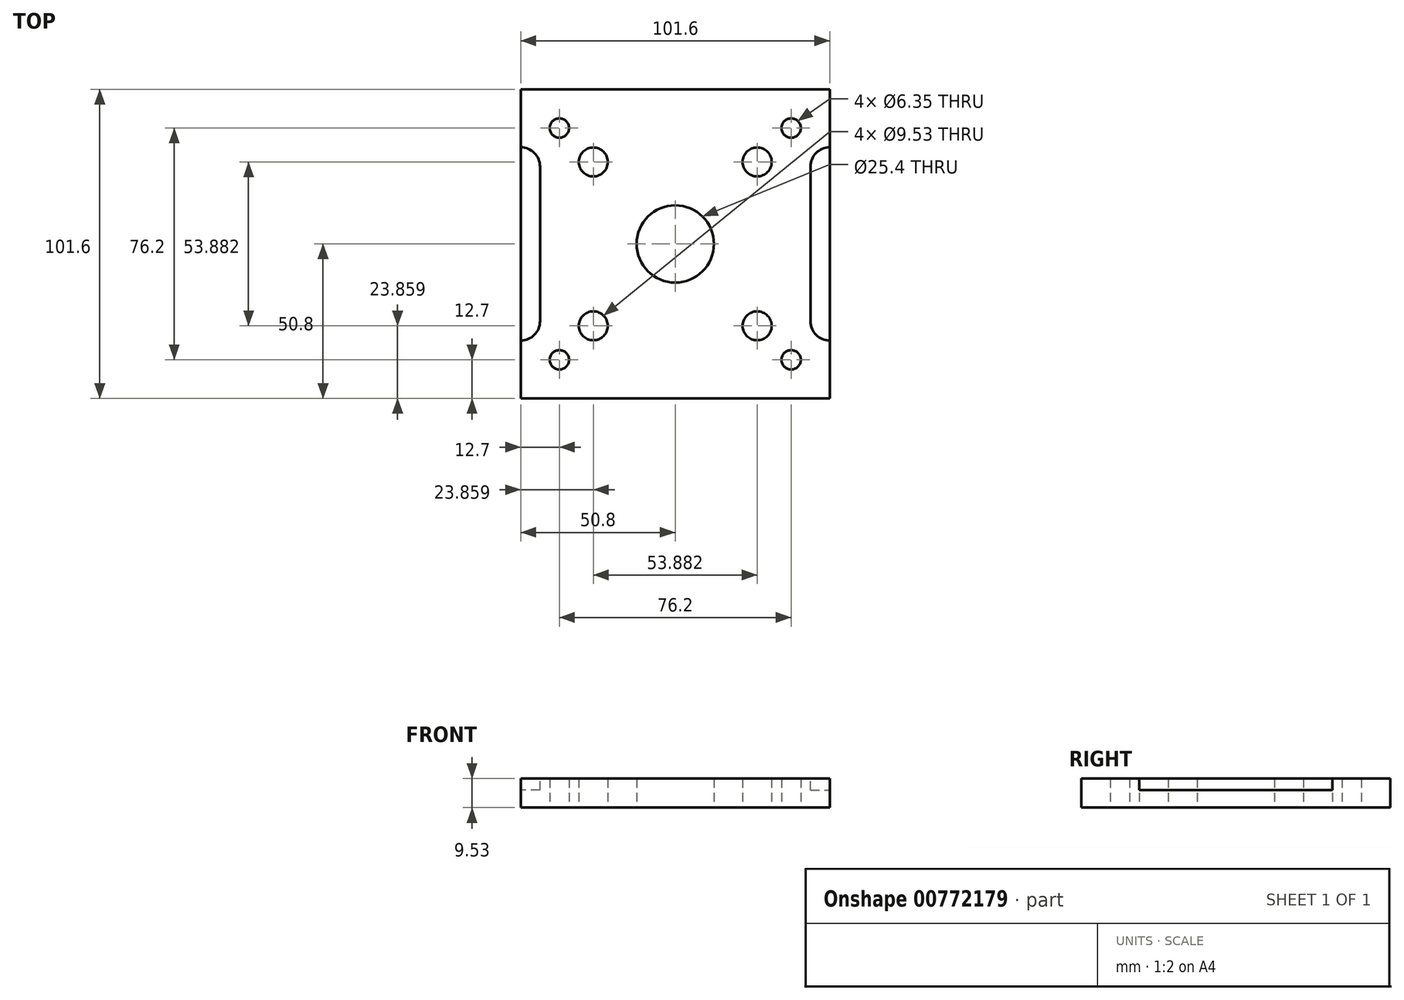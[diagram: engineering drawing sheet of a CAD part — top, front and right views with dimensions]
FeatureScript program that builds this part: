
annotation { "Feature Type Name" : "Feature", "Feature Type Description" : "" }
export const myFeature = defineFeature(function(context is Context, id is Id, definition is map)
    precondition{}
    {
        {
            var Q0;
            Q0=qCreatedBy(makeId("Top.planeOp"),FACE);
            var sketch = newSketch(context, id + "F0", { "sketchPlane" : qUnion([Q0])});
            skLineSegment(sketch, "E0.bottom", {"start": v(0, 0) * mm, "end": v(101.6, 0) * mm});
            skLineSegment(sketch, "E0.top", {"start": v(0, 101.6) * mm, "end": v(101.6, 101.6) * mm});
            skLineSegment(sketch, "E0.left", {"start": v(0, 0) * mm, "end": v(0, 101.6) * mm});
            skLineSegment(sketch, "E0.right", {"start": v(101.6, 0) * mm, "end": v(101.6, 101.6) * mm});
            skLineSegment(sketch, "E1", {"start": v(0, 101.6) * mm, "end": v(101.6, 0) * mm, "construction": true});
            skLineSegment(sketch, "E2", {"start": v(0, 0) * mm, "end": v(101.6, 101.6) * mm, "construction": true});
            skCircle(sketch, "E3", {"center": v(23.86, 77.74) * mm, "radius": 4.76 * mm});
            skCircle(sketch, "E4", {"center": v(77.74, 23.86) * mm, "radius": 4.76 * mm});
            skCircle(sketch, "E5", {"center": v(23.86, 23.86) * mm, "radius": 4.76 * mm});
            skCircle(sketch, "E6", {"center": v(77.74, 77.74) * mm, "radius": 4.76 * mm});
            skCircle(sketch, "E7", {"center": v(50.8, 50.8) * mm, "radius": 12.7 * mm});
            skCircle(sketch, "E8", {"center": v(12.7, 88.9) * mm, "radius": 3.18 * mm});
            skCircle(sketch, "E9", {"center": v(88.9, 88.9) * mm, "radius": 3.18 * mm});
            skCircle(sketch, "E10", {"center": v(88.9, 12.7) * mm, "radius": 3.18 * mm});
            skCircle(sketch, "E11", {"center": v(12.7, 12.7) * mm, "radius": 3.18 * mm});
            skSolve(sketch);
        }
        {
            var Q0;
            Q0=makeQuery(id+"F0.imprint","IMPRINT",FACE,{"disambiguationData":[TD([[makeQuery(id+"F0.imprint","IMPRINT",EDGE,{"derivedFrom":sQuery(id+"F0.wireOp",EDGE,"E0.bottom")}),1.0]])]});
            extrude(context, id + "F1", {"entities" : qUnion([Q0]), "depth" : 9.52 * mm, "offsetDistance" : 25.4 * mm});
        }
        {
            var Q0;
            Q0=makeQuery(id+"F1.opExtrude","CAP_FACE",FACE,{"disambiguationData":[OSD([sQuery(id+"F0.wireOp",EDGE,"E0.bottom"),sQuery(id+"F0.wireOp",EDGE,"E0.top"),sQuery(id+"F0.wireOp",EDGE,"E0.left"),sQuery(id+"F0.wireOp",EDGE,"E0.right"),sQuery(id+"F0.wireOp",EDGE,"E3"),sQuery(id+"F0.wireOp",EDGE,"E4"),sQuery(id+"F0.wireOp",EDGE,"E5"),sQuery(id+"F0.wireOp",EDGE,"E6"),sQuery(id+"F0.wireOp",EDGE,"E7"),sQuery(id+"F0.wireOp",EDGE,"E8"),sQuery(id+"F0.wireOp",EDGE,"E9"),sQuery(id+"F0.wireOp",EDGE,"E10"),sQuery(id+"F0.wireOp",EDGE,"E11")])],"isStart":false});
            var sketch = newSketch(context, id + "F2", { "sketchPlane" : qUnion([Q0])});
            skArc(sketch, "E12", {"start": v(6.35, 76.2) * mm, "mid": v(4.5, 80.7) * mm, "end": v(0, 82.55) * mm});
            skArc(sketch, "E13", {"start": v(0, 19.05) * mm, "mid": v(4.5, 20.9) * mm, "end": v(6.35, 25.4) * mm});
            skArc(sketch, "E14", {"start": v(95.25, 25.4) * mm, "mid": v(97.1, 20.9) * mm, "end": v(101.6, 19.05) * mm});
            skArc(sketch, "E15", {"start": v(101.6, 82.55) * mm, "mid": v(97.1, 80.7) * mm, "end": v(95.25, 76.2) * mm});
            skLineSegment(sketch, "E16", {"start": v(6.35, 76.2) * mm, "end": v(6.35, 25.4) * mm});
            skLineSegment(sketch, "E17", {"start": v(95.25, 25.4) * mm, "end": v(95.25, 76.2) * mm});
            skLineSegment(sketch, "E18.0.0", {"start": v(101.6, 101.6) * mm, "end": v(0, 101.6) * mm});
            skLineSegment(sketch, "E18.0.1", {"start": v(0, 101.6) * mm, "end": v(0, 0) * mm});
            skLineSegment(sketch, "E18.0.2", {"start": v(0, 0) * mm, "end": v(101.6, 0) * mm});
            skLineSegment(sketch, "E18.0.3", {"start": v(101.6, 0) * mm, "end": v(101.6, 101.6) * mm});
            skSolve(sketch);
        }
        {
            var Q0;
            {var subQ0=sQuery(id+"F2.wireOp",EDGE,"E12");var subQ1=makeQuery(id+"F1.opExtrude","CAP_EDGE",EDGE,{"disambiguationData":[OSD([sQuery(id+"F0.wireOp",EDGE,"E0.left")])],"isStart":false});var subQ2=makeQuery(id+"F2.imprint","INTERSECT",VERTEX,{"disambiguationData":[OD(0.0)],"derivedFrom":[subQ1,subQ0]});Q0=makeQuery(id+"F2.imprint","IMPRINT",FACE,{"disambiguationData":[TD([[makeQuery(id+"F2.imprint","IMPRINT",EDGE,{"disambiguationData":[TD([[subQ2,1.0]])],"derivedFrom":subQ0}),1.0]])]});}
            var Q1;
            {var subQ0=sQuery(id+"F2.wireOp",EDGE,"E15");var subQ1=makeQuery(id+"F1.opExtrude","CAP_EDGE",EDGE,{"disambiguationData":[OSD([sQuery(id+"F0.wireOp",EDGE,"E0.right")])],"isStart":false});var subQ2=makeQuery(id+"F2.imprint","INTERSECT",VERTEX,{"disambiguationData":[OD(0.0)],"derivedFrom":[subQ1,subQ0]});Q1=makeQuery(id+"F2.imprint","IMPRINT",FACE,{"disambiguationData":[TD([[makeQuery(id+"F2.imprint","IMPRINT",EDGE,{"disambiguationData":[TD([[subQ2,-1.0]])],"derivedFrom":subQ0}),1.0]])]});}
            var Q2;
            {var subQ0=sQuery(id+"F2.wireOp",EDGE,"E14");var subQ1=makeQuery(id+"F1.opExtrude","CAP_EDGE",EDGE,{"disambiguationData":[OSD([sQuery(id+"F0.wireOp",EDGE,"E0.right")])],"isStart":false});var subQ2=makeQuery(id+"F2.imprint","INTERSECT",VERTEX,{"disambiguationData":[OD(0.0)],"derivedFrom":[subQ1,subQ0]});Q2=makeQuery(id+"F2.imprint","IMPRINT",FACE,{"disambiguationData":[TD([[makeQuery(id+"F2.imprint","IMPRINT",EDGE,{"disambiguationData":[TD([[subQ2,1.0]])],"derivedFrom":subQ0}),1.0]])]});}
            var Q3;
            {var subQ0=sQuery(id+"F2.wireOp",EDGE,"E13");var subQ1=makeQuery(id+"F1.opExtrude","CAP_EDGE",EDGE,{"disambiguationData":[OSD([sQuery(id+"F0.wireOp",EDGE,"E0.left")])],"isStart":false});var subQ2=makeQuery(id+"F2.imprint","INTERSECT",VERTEX,{"disambiguationData":[OD(0.0)],"derivedFrom":[subQ1,subQ0]});Q3=makeQuery(id+"F2.imprint","IMPRINT",FACE,{"disambiguationData":[TD([[makeQuery(id+"F2.imprint","IMPRINT",EDGE,{"disambiguationData":[TD([[subQ2,-1.0]])],"derivedFrom":subQ0}),1.0]])]});}
            extrude(context, id + "F3", {"entities" : qUnion([Q0, Q1, Q2, Q3]), "operationType" : NewBodyOperationType.REMOVE, "oppositeDirection" : true, "depth" : 3.8 * mm, "offsetDistance" : 25.4 * mm});
        }
    });
